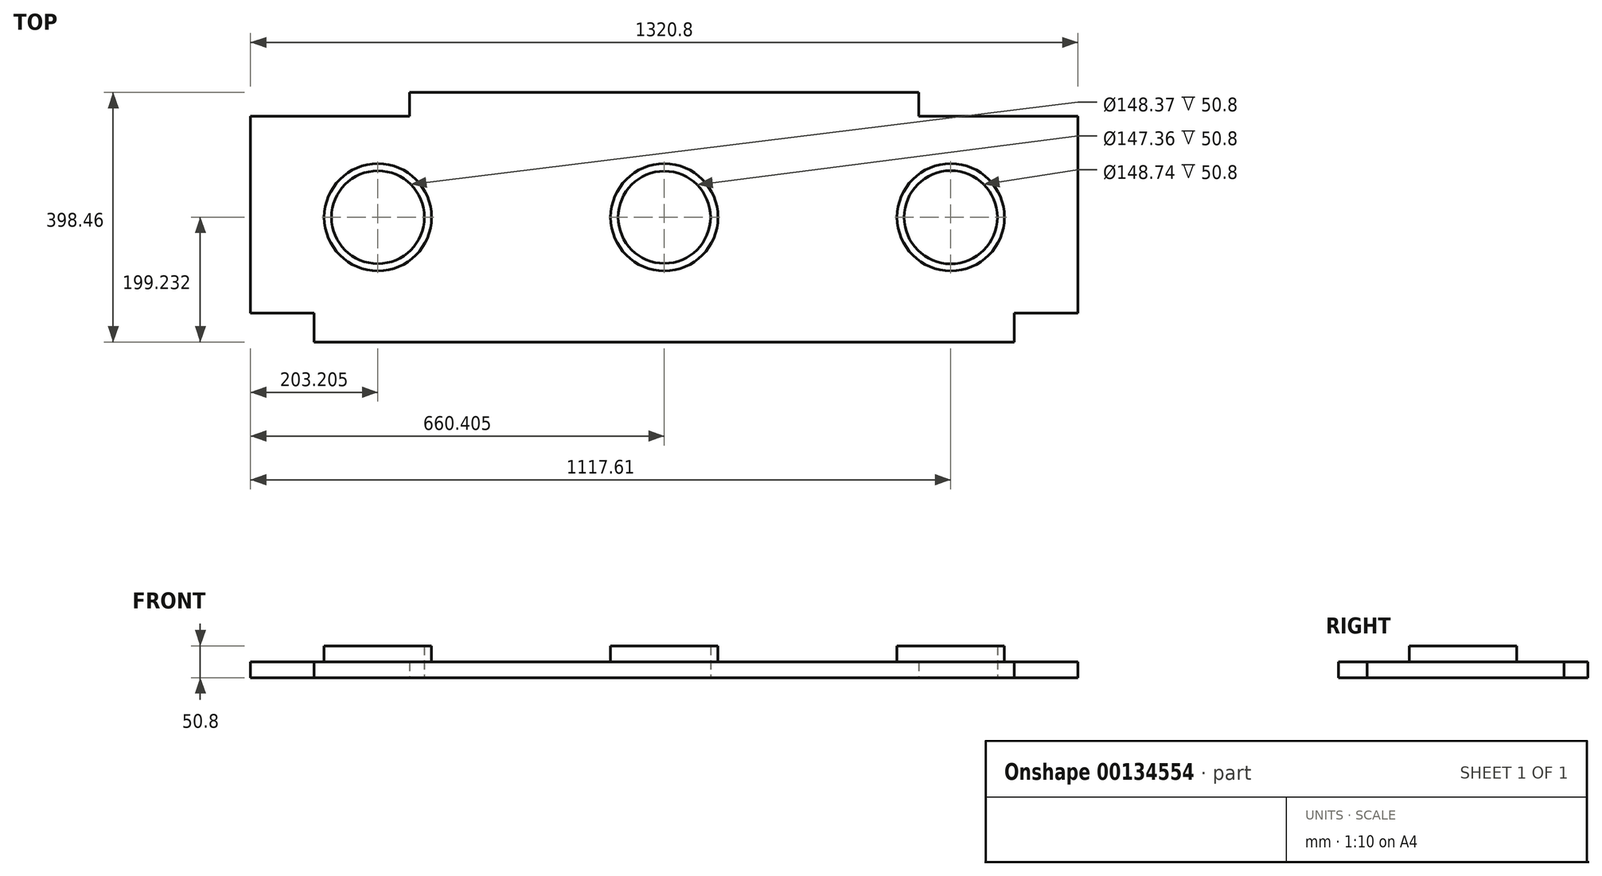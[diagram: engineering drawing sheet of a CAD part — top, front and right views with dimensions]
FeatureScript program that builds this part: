
annotation { "Feature Type Name" : "Feature", "Feature Type Description" : "" }
export const myFeature = defineFeature(function(context is Context, id is Id, definition is map)
    precondition{}
    {
        {
            var Q0;
            Q0=qCreatedBy(makeId("Top.planeOp"),FACE);
            var sketch = newSketch(context, id + "F0", { "sketchPlane" : qUnion([Q0])});
            skLineSegment(sketch, "E0", {"start": v(-60.36, 306.04) * mm, "end": v(-60.36, -8.28) * mm});
            skLineSegment(sketch, "E1", {"start": v(-60.36, -8.28) * mm, "end": v(41.24, -8.28) * mm});
            skLineSegment(sketch, "E2", {"start": v(41.24, -8.28) * mm, "end": v(41.24, -54.32) * mm});
            skLineSegment(sketch, "E3", {"start": v(41.24, -54.32) * mm, "end": v(1158.84, -54.32) * mm});
            skLineSegment(sketch, "E4", {"start": v(1158.84, -54.32) * mm, "end": v(1158.84, -8.28) * mm});
            skLineSegment(sketch, "E5", {"start": v(1158.84, -8.28) * mm, "end": v(1260.44, -8.28) * mm});
            skLineSegment(sketch, "E6", {"start": v(1260.44, -8.28) * mm, "end": v(1260.44, 306.04) * mm});
            skLineSegment(sketch, "E7", {"start": v(1260.44, 306.04) * mm, "end": v(1006.44, 306.04) * mm});
            skLineSegment(sketch, "E8", {"start": v(1006.44, 306.04) * mm, "end": v(1006.44, 344.14) * mm});
            skLineSegment(sketch, "E9", {"start": v(1006.44, 344.14) * mm, "end": v(193.64, 344.14) * mm});
            skLineSegment(sketch, "E10", {"start": v(193.64, 344.14) * mm, "end": v(193.64, 306.04) * mm});
            skLineSegment(sketch, "E11", {"start": v(193.64, 306.04) * mm, "end": v(-60.36, 306.04) * mm});
            skLineSegment(sketch, "E12", {"start": v(600.04, -54.32) * mm, "end": v(600.04, 344.14) * mm});
            skCircle(sketch, "E13", {"center": v(600.04, 144.91) * mm, "radius": 85.73 * mm});
            skCircle(sketch, "E14", {"center": v(600.04, 144.91) * mm, "radius": 73.68 * mm});
            skLineSegment(sketch, "E15", {"start": v(600.04, 144.91) * mm, "end": v(142.84, 144.91) * mm});
            skLineSegment(sketch, "E16", {"start": v(600.04, 144.91) * mm, "end": v(1057.24, 144.91) * mm});
            skCircle(sketch, "E17", {"center": v(142.84, 144.91) * mm, "radius": 85.73 * mm});
            skCircle(sketch, "E18", {"center": v(1057.24, 144.91) * mm, "radius": 85.73 * mm});
            skCircle(sketch, "E19", {"center": v(142.84, 144.91) * mm, "radius": 74.19 * mm});
            skCircle(sketch, "E20", {"center": v(1057.24, 144.91) * mm, "radius": 74.37 * mm});
            skSolve(sketch);
        }
        {
            var Q0;
            Q0 = qSketchRegion(id + "F0", true);
            extrude(context, id + "F1", {"entities" : qUnion([Q0]), "depth" : 25.4 * mm});
        }
        {
            var Q0;
            Q0=makeQuery(id+"F0.imprint","IMPRINT",FACE,{"disambiguationData":[TD([[makeQuery(id+"F0.imprint","IMPRINT",EDGE,{"derivedFrom":sQuery(id+"F0.wireOp",EDGE,"E17")}),1.0]])]});
            extrude(context, id + "F2", {"entities" : qUnion([Q0]), "operationType" : NewBodyOperationType.ADD, "depth" : 50.8 * mm});
        }
        {
            var Q0;
            {var subQ0=sQuery(id+"F0.wireOp",EDGE,"E13");var subQ1=sQuery(id+"F0.wireOp",EDGE,"E12");var subQ2=makeQuery(id+"F0.imprint","INTERSECT",VERTEX,{"disambiguationData":[OD(0.0)],"derivedFrom":[subQ1,subQ0]});Q0=makeQuery(id+"F0.imprint","IMPRINT",FACE,{"disambiguationData":[TD([[makeQuery(id+"F0.imprint","IMPRINT",EDGE,{"disambiguationData":[TD([[subQ2,-1.0]])],"derivedFrom":subQ1}),-1.0]])]});}
            var Q1;
            {var subQ0=sQuery(id+"F0.wireOp",EDGE,"E14");var subQ1=sQuery(id+"F0.wireOp",EDGE,"E12");var subQ2=makeQuery(id+"F0.imprint","INTERSECT",VERTEX,{"disambiguationData":[OD(1.0)],"derivedFrom":[subQ1,subQ0]});Q1=makeQuery(id+"F0.imprint","IMPRINT",FACE,{"disambiguationData":[TD([[makeQuery(id+"F0.imprint","IMPRINT",EDGE,{"disambiguationData":[TD([[subQ2,-1.0]])],"derivedFrom":subQ1}),-1.0]])]});}
            var Q2;
            {var subQ0=sQuery(id+"F0.wireOp",EDGE,"E14");var subQ1=sQuery(id+"F0.wireOp",EDGE,"E12");var subQ2=makeQuery(id+"F0.imprint","INTERSECT",VERTEX,{"disambiguationData":[OD(1.0)],"derivedFrom":[subQ1,subQ0]});Q2=makeQuery(id+"F0.imprint","IMPRINT",FACE,{"disambiguationData":[TD([[makeQuery(id+"F0.imprint","IMPRINT",EDGE,{"disambiguationData":[TD([[subQ2,-1.0]])],"derivedFrom":subQ1}),1.0]])]});}
            var Q3;
            {var subQ0=sQuery(id+"F0.wireOp",EDGE,"E13");var subQ1=sQuery(id+"F0.wireOp",EDGE,"E12");var subQ2=makeQuery(id+"F0.imprint","INTERSECT",VERTEX,{"disambiguationData":[OD(0.0)],"derivedFrom":[subQ1,subQ0]});Q3=makeQuery(id+"F0.imprint","IMPRINT",FACE,{"disambiguationData":[TD([[makeQuery(id+"F0.imprint","IMPRINT",EDGE,{"disambiguationData":[TD([[subQ2,-1.0]])],"derivedFrom":subQ1}),1.0]])]});}
            extrude(context, id + "F3", {"entities" : qUnion([Q0, Q1, Q2, Q3]), "operationType" : NewBodyOperationType.ADD, "depth" : 50.8 * mm});
        }
        {
            var Q0;
            Q0=makeQuery(id+"F0.imprint","IMPRINT",FACE,{"disambiguationData":[TD([[makeQuery(id+"F0.imprint","IMPRINT",EDGE,{"derivedFrom":sQuery(id+"F0.wireOp",EDGE,"E18")}),1.0]])]});
            extrude(context, id + "F4", {"entities" : qUnion([Q0]), "operationType" : NewBodyOperationType.ADD, "depth" : 50.8 * mm});
        }
    });
